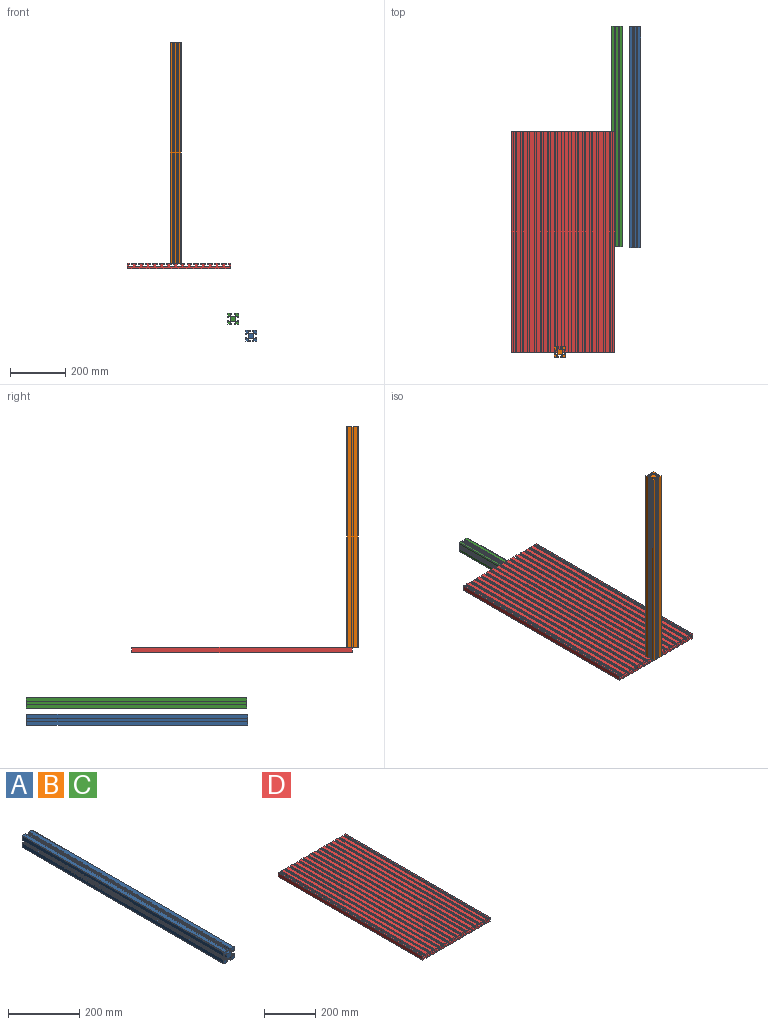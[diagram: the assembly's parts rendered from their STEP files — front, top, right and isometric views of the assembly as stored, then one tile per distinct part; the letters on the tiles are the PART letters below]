
ASSEMBLY  parts=4 mates=1
PART A: 106 faces, bbox 40x800x40 mm
  f0: cylinder r=1mm len=800mm, axis (0,-1,0), area 1256.6mm2, adj f1,f2,f104,f105
  f1: plane 800x13.75mm, normal (-1,0,0), area 11000mm2, adj f0,f2,f80,f105
  f2: plane 40x40mm, normal (0,1,0), area 889.3mm2, adj f0,f1,f3,f4,f5,f6,f7,f8
  f3: cylinder r=1mm len=800mm, axis (0,-1,0), area 1256.6mm2, adj f2,f4,f79,f105
  f4: plane 800x13.75mm, normal (-1,0,0), area 11000mm2, adj f2,f3,f19,f105
  f5: cylinder r=1mm len=800mm, axis (0,-1,0), area 1256.6mm2, adj f2,f6,f78,f105
  f6: plane 800x13.75mm, normal (1,0,0), area 11000mm2, adj f2,f5,f13,f105
  f7: cylinder r=1mm len=800mm, axis (0,-1,0), area 1256.6mm2, adj f2,f8,f30,f105
  f8: plane 800x13.75mm, normal (1,0,0), area 11000mm2, adj f2,f7,f11,f105
  f9: plane 800x1mm, normal (-0.71,0,0.71), area 1131.4mm2, adj f2,f10,f30,f105
  f10: plane 800x3mm, normal (-1,0,0), area 2400mm2, adj f2,f9,f26,f105
  f11: plane 800x1mm, normal (0.71,0,-0.71), area 1131.4mm2, adj f2,f8,f12,f105
  f12: plane 800x3mm, normal (0,0,-1), area 2400mm2, adj f2,f11,f74,f105
  f13: plane 800x1mm, normal (0.71,0,0.71), area 1131.4mm2, adj f2,f6,f14,f105
  f14: plane 800x3mm, normal (0,0,1), area 2400mm2, adj f2,f13,f36,f105
  f15: plane 800x1mm, normal (-0.71,0,-0.71), area 1131.4mm2, adj f2,f16,f78,f105
  f16: plane 800x3mm, normal (-1,0,0), area 2400mm2, adj f2,f15,f55,f105
  f17: plane 800x1mm, normal (0.71,0,-0.71), area 1131.4mm2, adj f2,f18,f79,f105
  f18: plane 800x3mm, normal (1,0,0), area 2400mm2, adj f2,f17,f45,f105
  f19: plane 800x1mm, normal (-0.71,0,0.71), area 1131.4mm2, adj f2,f4,f20,f105
  f20: plane 800x3mm, normal (0,0,1), area 2400mm2, adj f2,f19,f64,f105
  f21: cylinder r=0.9mm len=800mm, axis (0,-1,0), area 1005.3mm2, adj f2,f22,f29,f105
  f22: plane 800x4.61mm, normal (-1,0,0), area 3686.7mm2, adj f2,f21,f23,f105
  f23: cylinder r=3mm len=800mm, axis (0,-1,0), area 1885mm2, adj f2,f22,f24,f105
  f24: plane 800x0.53mm, normal (-0.71,0,0.71), area 604mm2, adj f2,f23,f25,f105
  f25: cylinder r=3mm len=800mm, axis (0,-1,0), area 1885mm2, adj f2,f24,f99,f105
  f26: plane 800x2.5mm, normal (0,0,-1), area 2000mm2, adj f2,f10,f27,f105
  f27: plane 800x1.01mm, normal (1,0,0), area 806.6mm2, adj f2,f26,f28,f105
  f28: cylinder r=1mm len=800mm, axis (0,-1,0), area 1396.3mm2, adj f2,f27,f29,f105
  f29: plane 800x0.93mm, normal (-0.17,0,-0.98), area 757.6mm2, adj f2,f21,f28,f105
  f30: plane 800x13.75mm, normal (0,0,1), area 11000mm2, adj f2,f7,f9,f105
  f31: cylinder r=0.9mm len=800mm, axis (0,-1,0), area 1005.3mm2, adj f2,f32,f39,f105
  f32: plane 800x4.61mm, normal (0,0,1), area 3686.7mm2, adj f2,f31,f33,f105
  f33: cylinder r=3mm len=800mm, axis (0,-1,0), area 1885mm2, adj f2,f32,f34,f105
  f34: plane 800x0.53mm, normal (0.71,0,0.71), area 604mm2, adj f2,f33,f35,f105
  f35: cylinder r=3mm len=800mm, axis (0,-1,0), area 1885mm2, adj f2,f34,f73,f105
  f36: plane 800x2.5mm, normal (-1,0,0), area 2000mm2, adj f2,f14,f37,f105
  f37: plane 800x1.01mm, normal (0,0,-1), area 806.6mm2, adj f2,f36,f38,f105
  f38: cylinder r=1mm len=800mm, axis (0,-1,0), area 1396.3mm2, adj f2,f37,f39,f105
  f39: plane 800x0.93mm, normal (-0.98,0,0.17), area 757.6mm2, adj f2,f31,f38,f105
  f40: cylinder r=0.9mm len=800mm, axis (0,-1,0), area 1005.3mm2, adj f2,f41,f48,f105
  f41: plane 800x4.61mm, normal (1,0,0), area 3686.7mm2, adj f2,f40,f42,f105
  f42: cylinder r=3mm len=800mm, axis (0,-1,0), area 1885mm2, adj f2,f41,f43,f105
  f43: plane 800x0.53mm, normal (0.71,0,-0.71), area 604mm2, adj f2,f42,f44,f105
  f44: cylinder r=3mm len=800mm, axis (0,-1,0), area 1885mm2, adj f2,f43,f54,f105
  f45: plane 800x2.5mm, normal (0,0,1), area 2000mm2, adj f2,f18,f46,f105
  f46: plane 800x1.01mm, normal (-1,0,0), area 806.6mm2, adj f2,f45,f47,f105
  f47: cylinder r=1mm len=800mm, axis (0,-1,0), area 1396.3mm2, adj f2,f46,f48,f105
  f48: plane 800x0.93mm, normal (0.17,0,0.98), area 757.6mm2, adj f2,f40,f47,f105
  f49: cylinder r=0.9mm len=800mm, axis (0,1,0), area 1005.3mm2, adj f2,f50,f58,f105
  f50: plane 800x4.61mm, normal (-1,0,0), area 3686.7mm2, adj f2,f49,f51,f105
  f51: cylinder r=3mm len=800mm, axis (0,1,0), area 1885mm2, adj f2,f50,f52,f105
  f52: plane 800x0.53mm, normal (-0.71,0,-0.71), area 604mm2, adj f2,f51,f53,f105
  f53: cylinder r=3mm len=800mm, axis (0,1,0), area 1885mm2, adj f2,f52,f54,f105
  f54: plane 800x12.13mm, normal (0,0,-1), area 9705.8mm2, adj f2,f44,f53,f105
  f55: plane 800x2.5mm, normal (0,0,1), area 2000mm2, adj f2,f16,f56,f105
  f56: plane 800x1.01mm, normal (1,0,0), area 806.6mm2, adj f2,f55,f57,f105
  f57: cylinder r=1mm len=800mm, axis (0,1,0), area 1396.3mm2, adj f2,f56,f58,f105
  f58: plane 800x0.93mm, normal (-0.17,0,0.98), area 757.6mm2, adj f2,f49,f57,f105
  f59: cylinder r=0.9mm len=800mm, axis (0,1,0), area 1005.3mm2, adj f2,f60,f67,f105
  f60: plane 800x4.61mm, normal (0,0,1), area 3686.7mm2, adj f2,f59,f61,f105
  f61: cylinder r=3mm len=800mm, axis (0,1,0), area 1885mm2, adj f2,f60,f62,f105
  f62: plane 800x0.53mm, normal (-0.71,0,0.71), area 604mm2, adj f2,f61,f63,f105
  f63: cylinder r=3mm len=800mm, axis (0,1,0), area 1885mm2, adj f2,f62,f88,f105
  f64: plane 800x2.5mm, normal (1,0,0), area 2000mm2, adj f2,f20,f65,f105
  f65: plane 800x1.01mm, normal (0,0,-1), area 806.6mm2, adj f2,f64,f66,f105
  f66: cylinder r=1mm len=800mm, axis (0,1,0), area 1396.3mm2, adj f2,f65,f67,f105
  f67: plane 800x0.93mm, normal (0.98,0,0.17), area 757.6mm2, adj f2,f59,f66,f105
  f68: cylinder r=0.9mm len=800mm, axis (0,1,0), area 1005.3mm2, adj f2,f69,f77,f105
  f69: plane 800x4.61mm, normal (0,0,-1), area 3686.7mm2, adj f2,f68,f70,f105
  f70: cylinder r=3mm len=800mm, axis (0,1,0), area 1885mm2, adj f2,f69,f71,f105
  f71: plane 800x0.53mm, normal (0.71,0,-0.71), area 604mm2, adj f2,f70,f72,f105
  f72: cylinder r=3mm len=800mm, axis (0,1,0), area 1885mm2, adj f2,f71,f73,f105
  f73: plane 800x12.13mm, normal (1,0,0), area 9705.8mm2, adj f2,f35,f72,f105
  f74: plane 800x2.5mm, normal (-1,0,0), area 2000mm2, adj f2,f12,f75,f105
  f75: plane 800x1.01mm, normal (0,0,1), area 806.6mm2, adj f2,f74,f76,f105
  f76: cylinder r=1mm len=800mm, axis (0,1,0), area 1396.3mm2, adj f2,f75,f77,f105
  f77: plane 800x0.93mm, normal (-0.98,0,-0.17), area 757.6mm2, adj f2,f68,f76,f105
  f78: plane 800x13.75mm, normal (0,0,-1), area 11000mm2, adj f2,f5,f15,f105
  f79: plane 800x13.75mm, normal (0,0,-1), area 11000mm2, adj f2,f3,f17,f105
  f80: plane 800x1mm, normal (-0.71,0,-0.71), area 1131.4mm2, adj f1,f2,f89,f105
  f81: plane 800x1mm, normal (0.71,0,0.71), area 1131.4mm2, adj f2,f82,f104,f105
  f82: plane 800x3mm, normal (1,0,0), area 2400mm2, adj f2,f81,f100,f105
  f83: cylinder r=0.9mm len=800mm, axis (0,-1,0), area 1005.3mm2, adj f2,f84,f93,f105
  f84: plane 800x4.61mm, normal (0,0,-1), area 3686.7mm2, adj f2,f83,f85,f105
  f85: cylinder r=3mm len=800mm, axis (0,-1,0), area 1885mm2, adj f2,f84,f86,f105
  f86: plane 800x0.53mm, normal (-0.71,0,-0.71), area 604mm2, adj f2,f85,f87,f105
  f87: cylinder r=3mm len=800mm, axis (0,-1,0), area 1885mm2, adj f2,f86,f88,f105
  f88: plane 800x12.13mm, normal (-1,0,0), area 9705.8mm2, adj f2,f63,f87,f105
  f89: plane 800x3mm, normal (0,0,-1), area 2400mm2, adj f2,f80,f90,f105
  f90: plane 800x2.5mm, normal (1,0,0), area 2000mm2, adj f2,f89,f91,f105
  f91: plane 800x1.01mm, normal (0,0,1), area 806.6mm2, adj f2,f90,f92,f105
  f92: cylinder r=1mm len=800mm, axis (0,-1,0), area 1396.3mm2, adj f2,f91,f93,f105
  f93: plane 800x0.93mm, normal (0.98,0,-0.17), area 757.6mm2, adj f2,f83,f92,f105
  f94: cylinder r=0.9mm len=800mm, axis (0,1,0), area 1005.3mm2, adj f2,f95,f103,f105
  f95: plane 800x4.61mm, normal (1,0,0), area 3686.7mm2, adj f2,f94,f96,f105
  f96: cylinder r=3mm len=800mm, axis (0,1,0), area 1885mm2, adj f2,f95,f97,f105
  f97: plane 800x0.53mm, normal (0.71,0,0.71), area 604mm2, adj f2,f96,f98,f105
  f98: cylinder r=3mm len=800mm, axis (0,1,0), area 1885mm2, adj f2,f97,f99,f105
  f99: plane 800x12.13mm, normal (0,0,1), area 9705.8mm2, adj f2,f25,f98,f105
  f100: plane 800x2.5mm, normal (0,0,-1), area 2000mm2, adj f2,f82,f101,f105
  f101: plane 800x1.01mm, normal (-1,0,0), area 806.6mm2, adj f2,f100,f102,f105
  f102: cylinder r=1mm len=800mm, axis (0,1,0), area 1396.3mm2, adj f2,f101,f103,f105
  f103: plane 800x0.93mm, normal (0.17,0,-0.98), area 757.6mm2, adj f2,f94,f102,f105
  f104: plane 800x13.75mm, normal (0,0,1), area 11000mm2, adj f0,f2,f81,f105
  f105: plane 40x40mm, normal (0,-1,0), area 889.3mm2, adj f0,f1,f3,f4,f5,f6,f7,f8
PART B: same geometry as A
PART C: same geometry as A
PART D: 272 faces, bbox 375x800x20 mm
  f0: plane 800x1.62mm, normal (0.98,0,-0.21), area 1327.9mm2, adj f1,f269,f270,f271
  f1: cylinder r=1.5mm len=800mm, axis (0,1,0), area 1633.7mm2, adj f0,f2,f270,f271
  f2: plane 800x3.12mm, normal (0,0,-1), area 2496.4mm2, adj f1,f3,f270,f271
  f3: cylinder r=1.5mm len=800mm, axis (0,1,0), area 1633.7mm2, adj f2,f4,f270,f271
  f4: plane 800x1.62mm, normal (-0.98,0,-0.21), area 1327.9mm2, adj f3,f5,f270,f271
  f5: cylinder r=1.5mm len=800mm, axis (0,1,0), area 377.1mm2, adj f4,f6,f270,f271
  f6: plane 800x17.92mm, normal (0,0,-1), area 14334.9mm2, adj f5,f7,f270,f271
  f7: cylinder r=1.5mm len=800mm, axis (0,1,0), area 377.1mm2, adj f6,f8,f270,f271
  f8: plane 800x1.62mm, normal (0.98,0,-0.21), area 1327.9mm2, adj f7,f9,f270,f271
  f9: cylinder r=1.5mm len=800mm, axis (0,1,0), area 1633.7mm2, adj f8,f10,f270,f271
  f10: plane 800x3.12mm, normal (0,0,-1), area 2496.4mm2, adj f9,f11,f270,f271
  f11: cylinder r=1.5mm len=800mm, axis (0,1,0), area 1633.7mm2, adj f10,f12,f270,f271
  f12: plane 800x1.62mm, normal (-0.98,0,-0.21), area 1327.9mm2, adj f11,f13,f270,f271
  f13: cylinder r=1.5mm len=800mm, axis (0,1,0), area 377.1mm2, adj f12,f14,f270,f271
  f14: plane 800x17.92mm, normal (0,0,-1), area 14334.9mm2, adj f13,f15,f270,f271
  f15: cylinder r=1.5mm len=800mm, axis (0,1,0), area 377.1mm2, adj f14,f16,f270,f271
  f16: plane 800x1.62mm, normal (0.98,0,-0.21), area 1327.9mm2, adj f15,f17,f270,f271
  f17: cylinder r=1.5mm len=800mm, axis (0,1,0), area 1633.7mm2, adj f16,f18,f270,f271
  f18: plane 800x3.12mm, normal (0,0,-1), area 2496.4mm2, adj f17,f19,f270,f271
  f19: cylinder r=1.5mm len=800mm, axis (0,1,0), area 1633.7mm2, adj f18,f20,f270,f271
  f20: plane 800x1.62mm, normal (-0.98,0,-0.21), area 1327.9mm2, adj f19,f21,f270,f271
  f21: cylinder r=1.5mm len=800mm, axis (0,1,0), area 377.1mm2, adj f20,f22,f270,f271
  f22: plane 800x17.92mm, normal (0,0,-1), area 14334.9mm2, adj f21,f23,f270,f271
  f23: cylinder r=1.5mm len=800mm, axis (0,1,0), area 377.1mm2, adj f22,f24,f270,f271
  f24: plane 800x1.62mm, normal (0.98,0,-0.21), area 1327.9mm2, adj f23,f25,f270,f271
  f25: cylinder r=1.5mm len=800mm, axis (0,1,0), area 1633.7mm2, adj f24,f26,f270,f271
  f26: plane 800x3.12mm, normal (0,0,-1), area 2496.4mm2, adj f25,f27,f270,f271
  f27: cylinder r=1.5mm len=800mm, axis (0,1,0), area 1633.7mm2, adj f26,f28,f270,f271
  f28: plane 800x1.62mm, normal (-0.98,0,-0.21), area 1327.9mm2, adj f27,f29,f270,f271
  f29: cylinder r=1.5mm len=800mm, axis (0,1,0), area 377.1mm2, adj f28,f30,f270,f271
  f30: plane 800x17.92mm, normal (0,0,-1), area 14334.9mm2, adj f29,f31,f270,f271
  f31: cylinder r=1.5mm len=800mm, axis (0,1,0), area 377.1mm2, adj f30,f32,f270,f271
  f32: plane 800x1.62mm, normal (0.98,0,-0.21), area 1327.9mm2, adj f31,f33,f270,f271
  f33: cylinder r=1.5mm len=800mm, axis (0,1,0), area 1633.7mm2, adj f32,f34,f270,f271
  f34: plane 800x3.12mm, normal (0,0,-1), area 2496.4mm2, adj f33,f35,f270,f271
  f35: cylinder r=1.5mm len=800mm, axis (0,1,0), area 1633.7mm2, adj f34,f36,f270,f271
  f36: plane 800x1.62mm, normal (-0.98,0,-0.21), area 1327.9mm2, adj f35,f37,f270,f271
  f37: cylinder r=1.5mm len=800mm, axis (0,1,0), area 377.1mm2, adj f36,f38,f270,f271
  f38: plane 800x17.92mm, normal (0,0,-1), area 14334.9mm2, adj f37,f39,f270,f271
  f39: cylinder r=1.5mm len=800mm, axis (0,1,0), area 377.1mm2, adj f38,f40,f270,f271
  f40: plane 800x1.62mm, normal (0.98,0,-0.21), area 1327.9mm2, adj f39,f41,f270,f271
  f41: cylinder r=1.5mm len=800mm, axis (0,1,0), area 1633.7mm2, adj f40,f42,f270,f271
  f42: plane 800x3.12mm, normal (0,0,-1), area 2496.4mm2, adj f41,f43,f270,f271
  f43: cylinder r=1.5mm len=800mm, axis (0,1,0), area 1633.7mm2, adj f42,f44,f270,f271
  f44: plane 800x1.62mm, normal (-0.98,0,-0.21), area 1327.9mm2, adj f43,f45,f270,f271
  f45: cylinder r=1.5mm len=800mm, axis (0,1,0), area 377.1mm2, adj f44,f46,f270,f271
  f46: plane 800x17.92mm, normal (0,0,-1), area 14334.9mm2, adj f45,f47,f270,f271
  f47: cylinder r=1.5mm len=800mm, axis (0,1,0), area 377.1mm2, adj f46,f48,f270,f271
  f48: plane 800x1.62mm, normal (0.98,0,-0.21), area 1327.9mm2, adj f47,f49,f270,f271
  f49: cylinder r=1.5mm len=800mm, axis (0,1,0), area 1633.7mm2, adj f48,f50,f270,f271
  f50: plane 800x3.12mm, normal (0,0,-1), area 2496.4mm2, adj f49,f51,f270,f271
  f51: cylinder r=1.5mm len=800mm, axis (0,1,0), area 1633.7mm2, adj f50,f52,f270,f271
  f52: plane 800x1.62mm, normal (-0.98,0,-0.21), area 1327.9mm2, adj f51,f53,f270,f271
  f53: cylinder r=1.5mm len=800mm, axis (0,1,0), area 377.1mm2, adj f52,f54,f270,f271
  f54: plane 800x17.92mm, normal (0,0,-1), area 14334.9mm2, adj f53,f55,f270,f271
  f55: cylinder r=1.5mm len=800mm, axis (0,1,0), area 377.1mm2, adj f54,f56,f270,f271
  f56: plane 800x1.62mm, normal (0.98,0,-0.21), area 1327.9mm2, adj f55,f57,f270,f271
  f57: cylinder r=1.5mm len=800mm, axis (0,1,0), area 1633.7mm2, adj f56,f58,f270,f271
  f58: plane 800x3.12mm, normal (0,0,-1), area 2496.4mm2, adj f57,f59,f270,f271
  f59: cylinder r=1.5mm len=800mm, axis (0,1,0), area 1633.7mm2, adj f58,f60,f270,f271
  f60: plane 800x1.62mm, normal (-0.98,0,-0.21), area 1327.9mm2, adj f59,f61,f270,f271
  f61: cylinder r=1.5mm len=800mm, axis (0,1,0), area 377.1mm2, adj f60,f62,f270,f271
  f62: plane 800x17.92mm, normal (0,0,-1), area 14334.9mm2, adj f61,f63,f270,f271
  f63: cylinder r=1.5mm len=800mm, axis (0,1,0), area 377.1mm2, adj f62,f64,f270,f271
  f64: plane 800x1.62mm, normal (0.98,0,-0.21), area 1327.9mm2, adj f63,f65,f270,f271
  f65: cylinder r=1.5mm len=800mm, axis (0,1,0), area 1633.7mm2, adj f64,f66,f270,f271
  f66: plane 800x3.12mm, normal (0,0,-1), area 2496.4mm2, adj f65,f67,f270,f271
  f67: cylinder r=1.5mm len=800mm, axis (0,1,0), area 1633.7mm2, adj f66,f68,f270,f271
  f68: plane 800x1.62mm, normal (-0.98,0,-0.21), area 1327.9mm2, adj f67,f69,f270,f271
  f69: cylinder r=1.5mm len=800mm, axis (0,1,0), area 377.1mm2, adj f68,f70,f270,f271
  f70: plane 800x17.92mm, normal (0,0,-1), area 14334.9mm2, adj f69,f71,f270,f271
  f71: cylinder r=1.5mm len=800mm, axis (0,1,0), area 377.1mm2, adj f70,f72,f270,f271
  f72: plane 800x1.62mm, normal (0.98,0,-0.21), area 1327.9mm2, adj f71,f73,f270,f271
  f73: cylinder r=1.5mm len=800mm, axis (0,1,0), area 1633.7mm2, adj f72,f74,f270,f271
  f74: plane 800x3.12mm, normal (0,0,-1), area 2496.4mm2, adj f73,f75,f270,f271
  f75: cylinder r=1.5mm len=800mm, axis (0,1,0), area 1633.7mm2, adj f74,f76,f270,f271
  f76: plane 800x1.62mm, normal (-0.98,0,-0.21), area 1327.9mm2, adj f75,f77,f270,f271
  f77: cylinder r=1.5mm len=800mm, axis (0,1,0), area 377.1mm2, adj f76,f78,f270,f271
  f78: plane 800x17.92mm, normal (0,0,-1), area 14334.9mm2, adj f77,f79,f270,f271
  f79: cylinder r=1.5mm len=800mm, axis (0,1,0), area 377.1mm2, adj f78,f80,f270,f271
  f80: plane 800x1.62mm, normal (0.98,0,-0.21), area 1327.9mm2, adj f79,f81,f270,f271
  f81: cylinder r=1.5mm len=800mm, axis (0,1,0), area 1633.7mm2, adj f80,f82,f270,f271
  f82: plane 800x3.12mm, normal (0,0,-1), area 2496.4mm2, adj f81,f83,f270,f271
  f83: cylinder r=1.5mm len=800mm, axis (0,1,0), area 1633.7mm2, adj f82,f84,f270,f271
  f84: plane 800x1.62mm, normal (-0.98,0,-0.21), area 1327.9mm2, adj f83,f85,f270,f271
  f85: cylinder r=1.5mm len=800mm, axis (0,1,0), area 377.1mm2, adj f84,f86,f270,f271
  f86: plane 800x20.46mm, normal (0,0,-1), area 16367.4mm2, adj f85,f87,f270,f271
  f87: plane 800x1mm, normal (0.71,0,-0.71), area 1131.4mm2, adj f86,f88,f270,f271
  f88: plane 800x18mm, normal (1,0,0), area 14400mm2, adj f87,f89,f270,f271
  f89: plane 800x1mm, normal (0.71,0,0.71), area 1131.4mm2, adj f88,f90,f270,f271
  f90: plane 800x6.45mm, normal (0,0,1), area 5160mm2, adj f89,f91,f270,f271
  f91: plane 800x1mm, normal (-0.71,0,0.71), area 1131.4mm2, adj f90,f92,f270,f271
  f92: plane 800x4mm, normal (-1,0,0), area 3200mm2, adj f91,f93,f270,f271
  f93: plane 800x3.2mm, normal (0,0,-1), area 2560mm2, adj f92,f94,f270,f271
  f94: plane 800x7mm, normal (-1,0,0), area 5600mm2, adj f93,f95,f270,f271
  f95: plane 800x14.5mm, normal (0,0,1), area 11600mm2, adj f94,f96,f270,f271
  f96: plane 800x7mm, normal (1,0,0), area 5600mm2, adj f95,f97,f270,f271
  f97: plane 800x3.2mm, normal (0,0,-1), area 2560mm2, adj f96,f98,f270,f271
  f98: plane 800x4mm, normal (1,0,0), area 3200mm2, adj f97,f99,f270,f271
  f99: plane 800x1mm, normal (0.71,0,0.71), area 1131.4mm2, adj f98,f100,f270,f271
  f100: plane 800x14.9mm, normal (0,0,1), area 11920mm2, adj f99,f101,f270,f271
  f101: plane 800x1mm, normal (-0.71,0,0.71), area 1131.4mm2, adj f100,f102,f270,f271
  f102: plane 800x4mm, normal (-1,0,0), area 3200mm2, adj f101,f103,f270,f271
  f103: plane 800x3.2mm, normal (0,0,-1), area 2560mm2, adj f102,f104,f270,f271
  f104: plane 800x7mm, normal (-1,0,0), area 5600mm2, adj f103,f105,f270,f271
  f105: plane 800x14.5mm, normal (0,0,1), area 11600mm2, adj f104,f106,f270,f271
  f106: plane 800x7mm, normal (1,0,0), area 5600mm2, adj f105,f107,f270,f271
  f107: plane 800x3.2mm, normal (0,0,-1), area 2560mm2, adj f106,f108,f270,f271
  f108: plane 800x4mm, normal (1,0,0), area 3200mm2, adj f107,f109,f270,f271
  f109: plane 800x1mm, normal (0.71,0,0.71), area 1131.4mm2, adj f108,f110,f270,f271
  f110: plane 800x14.9mm, normal (0,0,1), area 11920mm2, adj f109,f111,f270,f271
  f111: plane 800x1mm, normal (-0.71,0,0.71), area 1131.4mm2, adj f110,f112,f270,f271
  f112: plane 800x4mm, normal (-1,0,0), area 3200mm2, adj f111,f113,f270,f271
  f113: plane 800x3.2mm, normal (0,0,-1), area 2560mm2, adj f112,f114,f270,f271
  f114: plane 800x7mm, normal (-1,0,0), area 5600mm2, adj f113,f115,f270,f271
  f115: plane 800x14.5mm, normal (0,0,1), area 11600mm2, adj f114,f116,f270,f271
  f116: plane 800x7mm, normal (1,0,0), area 5600mm2, adj f115,f117,f270,f271
  f117: plane 800x3.2mm, normal (0,0,-1), area 2560mm2, adj f116,f118,f270,f271
  f118: plane 800x4mm, normal (1,0,0), area 3200mm2, adj f117,f119,f270,f271
  f119: plane 800x1mm, normal (0.71,0,0.71), area 1131.4mm2, adj f118,f120,f270,f271
  f120: plane 800x14.9mm, normal (0,0,1), area 11920mm2, adj f119,f121,f270,f271
  f121: plane 800x1mm, normal (-0.71,0,0.71), area 1131.4mm2, adj f120,f122,f270,f271
  f122: plane 800x4mm, normal (-1,0,0), area 3200mm2, adj f121,f123,f270,f271
  f123: plane 800x3.2mm, normal (0,0,-1), area 2560mm2, adj f122,f124,f270,f271
  f124: plane 800x7mm, normal (-1,0,0), area 5600mm2, adj f123,f125,f270,f271
  f125: plane 800x14.5mm, normal (0,0,1), area 11600mm2, adj f124,f126,f270,f271
  f126: plane 800x7mm, normal (1,0,0), area 5600mm2, adj f125,f127,f270,f271
  f127: plane 800x3.2mm, normal (0,0,-1), area 2560mm2, adj f126,f128,f270,f271
  f128: plane 800x4mm, normal (1,0,0), area 3200mm2, adj f127,f129,f270,f271
  f129: plane 800x1mm, normal (0.71,0,0.71), area 1131.4mm2, adj f128,f130,f270,f271
  f130: plane 800x14.9mm, normal (0,0,1), area 11920mm2, adj f129,f131,f270,f271
  f131: plane 800x1mm, normal (-0.71,0,0.71), area 1131.4mm2, adj f130,f132,f270,f271
  f132: plane 800x4mm, normal (-1,0,0), area 3200mm2, adj f131,f133,f270,f271
  f133: plane 800x3.2mm, normal (0,0,-1), area 2560mm2, adj f132,f134,f270,f271
  f134: plane 800x7mm, normal (-1,0,0), area 5600mm2, adj f133,f135,f270,f271
  f135: plane 800x14.5mm, normal (0,0,1), area 11600mm2, adj f134,f136,f270,f271
  f136: plane 800x7mm, normal (1,0,0), area 5600mm2, adj f135,f137,f270,f271
  f137: plane 800x3.2mm, normal (0,0,-1), area 2560mm2, adj f136,f138,f270,f271
  f138: plane 800x4mm, normal (1,0,0), area 3200mm2, adj f137,f139,f270,f271
  f139: plane 800x1mm, normal (0.71,0,0.71), area 1131.4mm2, adj f138,f140,f270,f271
  f140: plane 800x14.9mm, normal (0,0,1), area 11920mm2, adj f139,f141,f270,f271
  f141: plane 800x1mm, normal (-0.71,0,0.71), area 1131.4mm2, adj f140,f142,f270,f271
  f142: plane 800x4mm, normal (-1,0,0), area 3200mm2, adj f141,f143,f270,f271
  f143: plane 800x3.2mm, normal (0,0,-1), area 2560mm2, adj f142,f144,f270,f271
  f144: plane 800x7mm, normal (-1,0,0), area 5600mm2, adj f143,f145,f270,f271
  f145: plane 800x14.5mm, normal (0,0,1), area 11600mm2, adj f144,f146,f270,f271
  f146: plane 800x7mm, normal (1,0,0), area 5600mm2, adj f145,f147,f270,f271
  f147: plane 800x3.2mm, normal (0,0,-1), area 2560mm2, adj f146,f148,f270,f271
  f148: plane 800x4mm, normal (1,0,0), area 3200mm2, adj f147,f149,f270,f271
  f149: plane 800x1mm, normal (0.71,0,0.71), area 1131.4mm2, adj f148,f150,f270,f271
  f150: plane 800x14.9mm, normal (0,0,1), area 11920mm2, adj f149,f151,f270,f271
  f151: plane 800x1mm, normal (-0.71,0,0.71), area 1131.4mm2, adj f150,f152,f270,f271
  f152: plane 800x4mm, normal (-1,0,0), area 3200mm2, adj f151,f153,f270,f271
  f153: plane 800x3.2mm, normal (0,0,-1), area 2560mm2, adj f152,f154,f270,f271
  f154: plane 800x7mm, normal (-1,0,0), area 5600mm2, adj f153,f155,f270,f271
  f155: plane 800x14.5mm, normal (0,0,1), area 11600mm2, adj f154,f156,f270,f271
  f156: plane 800x7mm, normal (1,0,0), area 5600mm2, adj f155,f157,f270,f271
  f157: plane 800x3.2mm, normal (0,0,-1), area 2560mm2, adj f156,f158,f270,f271
  f158: plane 800x4mm, normal (1,0,0), area 3200mm2, adj f157,f159,f270,f271
  f159: plane 800x1mm, normal (0.71,0,0.71), area 1131.4mm2, adj f158,f160,f270,f271
  f160: plane 800x14.9mm, normal (0,0,1), area 11920mm2, adj f159,f161,f270,f271
  f161: plane 800x1mm, normal (-0.71,0,0.71), area 1131.4mm2, adj f160,f162,f270,f271
  f162: plane 800x4mm, normal (-1,0,0), area 3200mm2, adj f161,f163,f270,f271
  f163: plane 800x3.2mm, normal (0,0,-1), area 2560mm2, adj f162,f164,f270,f271
  f164: plane 800x7mm, normal (-1,0,0), area 5600mm2, adj f163,f165,f270,f271
  f165: plane 800x14.5mm, normal (0,0,1), area 11600mm2, adj f164,f166,f270,f271
  f166: plane 800x7mm, normal (1,0,0), area 5600mm2, adj f165,f167,f270,f271
  f167: plane 800x3.2mm, normal (0,0,-1), area 2560mm2, adj f166,f168,f270,f271
  f168: plane 800x4mm, normal (1,0,0), area 3200mm2, adj f167,f169,f270,f271
  f169: plane 800x1mm, normal (0.71,0,0.71), area 1131.4mm2, adj f168,f170,f270,f271
  f170: plane 800x14.9mm, normal (0,0,1), area 11920mm2, adj f169,f171,f270,f271
  f171: plane 800x1mm, normal (-0.71,0,0.71), area 1131.4mm2, adj f170,f172,f270,f271
  f172: plane 800x4mm, normal (-1,0,0), area 3200mm2, adj f171,f173,f270,f271
  f173: plane 800x3.2mm, normal (0,0,-1), area 2560mm2, adj f172,f174,f270,f271
  f174: plane 800x7mm, normal (-1,0,0), area 5600mm2, adj f173,f175,f270,f271
  f175: plane 800x14.5mm, normal (0,0,1), area 11600mm2, adj f174,f176,f270,f271
  f176: plane 800x7mm, normal (1,0,0), area 5600mm2, adj f175,f177,f270,f271
  f177: plane 800x3.2mm, normal (0,0,-1), area 2560mm2, adj f176,f178,f270,f271
  f178: plane 800x4mm, normal (1,0,0), area 3200mm2, adj f177,f179,f270,f271
  f179: plane 800x1mm, normal (0.71,0,0.71), area 1131.4mm2, adj f178,f180,f270,f271
  f180: plane 800x14.9mm, normal (0,0,1), area 11920mm2, adj f179,f181,f270,f271
  f181: plane 800x1mm, normal (-0.71,0,0.71), area 1131.4mm2, adj f180,f182,f270,f271
  f182: plane 800x4mm, normal (-1,0,0), area 3200mm2, adj f181,f183,f270,f271
  f183: plane 800x3.2mm, normal (0,0,-1), area 2560mm2, adj f182,f184,f270,f271
  f184: plane 800x7mm, normal (-1,0,0), area 5600mm2, adj f183,f185,f270,f271
  f185: plane 800x14.5mm, normal (0,0,1), area 11600mm2, adj f184,f186,f270,f271
  f186: plane 800x7mm, normal (1,0,0), area 5600mm2, adj f185,f187,f270,f271
  f187: plane 800x3.2mm, normal (0,0,-1), area 2560mm2, adj f186,f188,f270,f271
  f188: plane 800x4mm, normal (1,0,0), area 3200mm2, adj f187,f189,f270,f271
  f189: plane 800x1mm, normal (0.71,0,0.71), area 1131.4mm2, adj f188,f190,f270,f271
  f190: plane 800x14.9mm, normal (0,0,1), area 11920mm2, adj f189,f191,f270,f271
  f191: plane 800x1mm, normal (-0.71,0,0.71), area 1131.4mm2, adj f190,f192,f270,f271
  f192: plane 800x4mm, normal (-1,0,0), area 3200mm2, adj f191,f193,f270,f271
  f193: plane 800x3.2mm, normal (0,0,-1), area 2560mm2, adj f192,f194,f270,f271
  f194: plane 800x7mm, normal (-1,0,0), area 5600mm2, adj f193,f195,f270,f271
  f195: plane 800x14.5mm, normal (0,0,1), area 11600mm2, adj f194,f196,f270,f271
  f196: plane 800x7mm, normal (1,0,0), area 5600mm2, adj f195,f197,f270,f271
  f197: plane 800x3.2mm, normal (0,0,-1), area 2560mm2, adj f196,f198,f270,f271
  f198: plane 800x4mm, normal (1,0,0), area 3200mm2, adj f197,f199,f270,f271
  f199: plane 800x1mm, normal (0.71,0,0.71), area 1131.4mm2, adj f198,f200,f270,f271
  f200: plane 800x14.9mm, normal (0,0,1), area 11920mm2, adj f199,f201,f270,f271
  f201: plane 800x1mm, normal (-0.71,0,0.71), area 1131.4mm2, adj f200,f202,f270,f271
  f202: plane 800x4mm, normal (-1,0,0), area 3200mm2, adj f201,f203,f270,f271
  f203: plane 800x3.2mm, normal (0,0,-1), area 2560mm2, adj f202,f204,f270,f271
  f204: plane 800x7mm, normal (-1,0,0), area 5600mm2, adj f203,f205,f270,f271
  f205: plane 800x14.5mm, normal (0,0,1), area 11600mm2, adj f204,f206,f270,f271
  f206: plane 800x7mm, normal (1,0,0), area 5600mm2, adj f205,f207,f270,f271
  f207: plane 800x3.2mm, normal (0,0,-1), area 2560mm2, adj f206,f208,f270,f271
  f208: plane 800x4mm, normal (1,0,0), area 3200mm2, adj f207,f209,f270,f271
  f209: plane 800x1mm, normal (0.71,0,0.71), area 1131.4mm2, adj f208,f210,f270,f271
  f210: plane 800x14.9mm, normal (0,0,1), area 11920mm2, adj f209,f211,f270,f271
  f211: plane 800x1mm, normal (-0.71,0,0.71), area 1131.4mm2, adj f210,f212,f270,f271
  f212: plane 800x4mm, normal (-1,0,0), area 3200mm2, adj f211,f213,f270,f271
  f213: plane 800x3.2mm, normal (0,0,-1), area 2560mm2, adj f212,f214,f270,f271
  f214: plane 800x7mm, normal (-1,0,0), area 5600mm2, adj f213,f215,f270,f271
  f215: plane 800x14.5mm, normal (0,0,1), area 11600mm2, adj f214,f216,f270,f271
  f216: plane 800x7mm, normal (1,0,0), area 5600mm2, adj f215,f217,f270,f271
  f217: plane 800x3.2mm, normal (0,0,-1), area 2560mm2, adj f216,f218,f270,f271
  f218: plane 800x4mm, normal (1,0,0), area 3200mm2, adj f217,f219,f270,f271
  f219: plane 800x1mm, normal (0.71,0,0.71), area 1131.4mm2, adj f218,f220,f270,f271
  f220: plane 800x14.9mm, normal (0,0,1), area 11920mm2, adj f219,f221,f270,f271
  f221: plane 800x1mm, normal (-0.71,0,0.71), area 1131.4mm2, adj f220,f222,f270,f271
  f222: plane 800x4mm, normal (-1,0,0), area 3200mm2, adj f221,f223,f270,f271
  f223: plane 800x3.2mm, normal (0,0,-1), area 2560mm2, adj f222,f224,f270,f271
  f224: plane 800x7mm, normal (-1,0,0), area 5600mm2, adj f223,f225,f270,f271
  f225: plane 800x14.5mm, normal (0,0,1), area 11600mm2, adj f224,f226,f270,f271
  f226: plane 800x7mm, normal (1,0,0), area 5600mm2, adj f225,f227,f270,f271
  f227: plane 800x3.2mm, normal (0,0,-1), area 2560mm2, adj f226,f228,f270,f271
  f228: plane 800x4mm, normal (1,0,0), area 3200mm2, adj f227,f229,f270,f271
  f229: plane 800x1mm, normal (0.71,0,0.71), area 1131.4mm2, adj f228,f230,f270,f271
  f230: plane 800x14.9mm, normal (0,0,1), area 11920mm2, adj f229,f231,f270,f271
  f231: plane 800x1mm, normal (-0.71,0,0.71), area 1131.4mm2, adj f230,f232,f270,f271
  f232: plane 800x4mm, normal (-1,0,0), area 3200mm2, adj f231,f233,f270,f271
  f233: plane 800x3.2mm, normal (0,0,-1), area 2560mm2, adj f232,f234,f270,f271
  f234: plane 800x7mm, normal (-1,0,0), area 5600mm2, adj f233,f235,f270,f271
  f235: plane 800x14.5mm, normal (0,0,1), area 11600mm2, adj f234,f236,f270,f271
  f236: plane 800x7mm, normal (1,0,0), area 5600mm2, adj f235,f237,f270,f271
  f237: plane 800x3.2mm, normal (0,0,-1), area 2560mm2, adj f236,f238,f270,f271
  f238: plane 800x4mm, normal (1,0,0), area 3200mm2, adj f237,f239,f270,f271
  f239: plane 800x1mm, normal (0.71,0,0.71), area 1131.4mm2, adj f238,f240,f270,f271
  f240: plane 800x6.45mm, normal (0,0,1), area 5160mm2, adj f239,f241,f270,f271
  f241: plane 800x1mm, normal (-0.71,0,0.71), area 1131.4mm2, adj f240,f242,f270,f271
  f242: plane 800x18mm, normal (-1,0,0), area 14400mm2, adj f241,f243,f270,f271
  f243: plane 800x1mm, normal (-0.71,0,-0.71), area 1131.4mm2, adj f242,f244,f270,f271
  f244: plane 800x20.46mm, normal (0,0,-1), area 16367.4mm2, adj f243,f245,f270,f271
  f245: cylinder r=1.5mm len=800mm, axis (0,1,0), area 377.1mm2, adj f244,f246,f270,f271
  f246: plane 800x1.62mm, normal (0.98,0,-0.21), area 1327.9mm2, adj f245,f247,f270,f271
  f247: cylinder r=1.5mm len=800mm, axis (0,1,0), area 1633.7mm2, adj f246,f248,f270,f271
  f248: plane 800x3.12mm, normal (0,0,-1), area 2496.4mm2, adj f247,f249,f270,f271
  f249: cylinder r=1.5mm len=800mm, axis (0,1,0), area 1633.7mm2, adj f248,f250,f270,f271
  f250: plane 800x1.62mm, normal (-0.98,0,-0.21), area 1327.9mm2, adj f249,f251,f270,f271
  f251: cylinder r=1.5mm len=800mm, axis (0,1,0), area 377.1mm2, adj f250,f252,f270,f271
  f252: plane 800x17.92mm, normal (0,0,-1), area 14334.9mm2, adj f251,f253,f270,f271
  f253: cylinder r=1.5mm len=800mm, axis (0,1,0), area 377.1mm2, adj f252,f254,f270,f271
  f254: plane 800x1.62mm, normal (0.98,0,-0.21), area 1327.9mm2, adj f253,f255,f270,f271
  f255: cylinder r=1.5mm len=800mm, axis (0,1,0), area 1633.7mm2, adj f254,f256,f270,f271
  f256: plane 800x3.12mm, normal (0,0,-1), area 2496.4mm2, adj f255,f257,f270,f271
  f257: cylinder r=1.5mm len=800mm, axis (0,1,0), area 1633.7mm2, adj f256,f258,f270,f271
  f258: plane 800x1.62mm, normal (-0.98,0,-0.21), area 1327.9mm2, adj f257,f259,f270,f271
  f259: cylinder r=1.5mm len=800mm, axis (0,1,0), area 377.1mm2, adj f258,f260,f270,f271
  f260: plane 800x17.92mm, normal (0,0,-1), area 14334.9mm2, adj f259,f261,f270,f271
  f261: cylinder r=1.5mm len=800mm, axis (0,1,0), area 377.1mm2, adj f260,f262,f270,f271
  f262: plane 800x1.62mm, normal (0.98,0,-0.21), area 1327.9mm2, adj f261,f263,f270,f271
  f263: cylinder r=1.5mm len=800mm, axis (0,1,0), area 1633.7mm2, adj f262,f264,f270,f271
  f264: plane 800x3.12mm, normal (0,0,-1), area 2496.4mm2, adj f263,f265,f270,f271
  f265: cylinder r=1.5mm len=800mm, axis (0,1,0), area 1633.7mm2, adj f264,f266,f270,f271
  f266: plane 800x1.62mm, normal (-0.98,0,-0.21), area 1327.9mm2, adj f265,f267,f270,f271
  f267: cylinder r=1.5mm len=800mm, axis (0,1,0), area 377.1mm2, adj f266,f268,f270,f271
  f268: plane 800x17.92mm, normal (0,0,-1), area 14334.9mm2, adj f267,f269,f270,f271
  f269: cylinder r=1.5mm len=800mm, axis (0,1,0), area 377.1mm2, adj f0,f268,f270,f271
  f270: plane 375x20mm, normal (0,-1,0), area 5076.9mm2, adj f0,f1,f2,f3,f4,f5,f6,f7
  f271: plane 375x20mm, normal (0,1,0), area 5076.9mm2, adj f0,f1,f2,f3,f4,f5,f6,f7
PLACE A t=(234.91,380.72,-232.35)mm
PLACE B rot(axis=(1,0,0),90deg) t=(-38.93,-798.97,830.24)mm
PLACE C t=(169.18,383.94,-170.6)mm
PLACE D t=(-26.43,1.03,20.24)mm
MATE fastened B.f105 <-> D.f170  axis (0,0,-1) through (-38.93,-798.97,30.24)mm
